# Revit family: Faucet-Single_Control-American_Standard-Colony_Pro-707500X_Series
name_source: partatom
category: Plumbing Fixtures
units: mm (PartAtom-declared; Revit-internal decimal feet)

## family parameters
Always vertical = No
Cut with Voids When Loaded = No
OmniClass Number = 23.45.55.14
OmniClass Title = Single Faucets
Part Type = Normal
Room Calculation Point = No
Round Connector Dimension = Use Diameter
Shared = Yes
Work Plane-Based = Yes

## types (12) — shared parameters
ADA Compliant = Yes
Assembly Code = D2020300
CEC Compliant = Yes
CW Connection = No
CWFU = 1.5
CalGreen Compliant = Yes
Compliance Certifications = These products meet or exceed the following codes and standards: ANSI A117.1, ASME A112.18.1,CSA B125.1,NSF 61/Section 9,NSF 372
Default Elevation = 0"
Drain Depth = 3"
Drain Width = 3"
Flow Rate = 1.2 gpm (4.5 L/min)
HW Connection = No
HWFU = 1.5
Height = 5 15/16"
Installation Type = Deck Mounted
Length = 6 3/8"
Manufacturer = American Standard
Product Documentation Link = https://americanstandard.box.com
Product Page URL = https://www.americanstandard-us.com
Revised Date = 09/23/2022
Tempered Water Connection = Yes
Tempered Water Connection Diameter = 3/8"
URL = http://www.americanstandard-us.com
Vent Connection = No
WFU = 2
Waste Connection = No
Width = 6"

## per-type parameters (varying)
| type | 50/50 Pop Up Drain | Description | Drain Visibility | Finish | Grid Drain | Material | Pop Up Drain | Pop-Up Hole & Rod |
| 7075000.002 | No | Colony® PRO 4-Inch Centerset Single-Handle Bathroom Faucet 1.2 gpm/4.5 L/min With Lever Handle | Yes | Metal-American Standard-002-Polished Chrome | No | Metal-American Standard-002-Polished Chrome | Yes | Yes |
| 7075000.295 | No | Colony® PRO 4-Inch Centerset Single-Handle Bathroom Faucet 1.2 gpm/4.5 L/min With Lever Handle | Yes | Metal-American Standard-295-Brushed Nickel | No | Metal-American Standard-295-Brushed Nickel | Yes | Yes |
| 7075000.278 | No | Colony® PRO 4-Inch Centerset Single-Handle Bathroom Faucet 1.2 gpm/4.5 L/min With Lever Handle | Yes | Metal-American Standard-278-Legacy Bronze | No | Metal-American Standard-278-Legacy Bronze | Yes | Yes |
| 7075002.002 | Yes | Colony® PRO 4-Inch Centerset Single-Handle Bathroom Faucet 1.2 gpm/4.5 Lpm With Lever Handle | Yes | Metal-American Standard-002-Polished Chrome | No | Metal-American Standard-002-Polished Chrome | No | Yes |
| 7075002.295 | Yes | Colony® PRO 4-Inch Centerset Single-Handle Bathroom Faucet 1.2 gpm/4.5 Lpm With Lever Handle | Yes | Metal-American Standard-295-Brushed Nickel | No | Metal-American Standard-295-Brushed Nickel | No | Yes |
| 7075002.278 | Yes | Colony® PRO 4-Inch Centerset Single-Handle Bathroom Faucet 1.2 gpm/4.5 Lpm With Lever Handle | Yes | Metal-American Standard-278-Legacy Bronze | No | Metal-American Standard-278-Legacy Bronze | No | Yes |
| 7075004.002 | No | Colony® PRO 4-Inch Centerset Single-Handle Bathroom Faucet 1.2 gpm/4.5 Lpm Less Drain With Lever Handle | No | Metal-American Standard-002-Polished Chrome | No | Metal-American Standard-002-Polished Chrome | No | No |
| 7075004.295 | No | Colony® PRO 4-Inch Centerset Single-Handle Bathroom Faucet 1.2 gpm/4.5 Lpm Less Drain With Lever Handle | No | Metal-American Standard-295-Brushed Nickel | No | Metal-American Standard-295-Brushed Nickel | No | No |
| 7075005.002 | No | Colony® PRO 4-Inch Centerset Single-Handle Bathroom Faucet 1.2 gpm/4.5 Lpm Less Drain With Lever Handle | No | Metal-American Standard-002-Polished Chrome | No | Metal-American Standard-002-Polished Chrome | No | Yes |
| 7075005.295 | No | Colony® PRO 4-Inch Centerset Single-Handle Bathroom Faucet 1.2 gpm/4.5 Lpm Less Drain With Lever Handle | No | Metal-American Standard-295-Brushed Nickel | No | Metal-American Standard-295-Brushed Nickel | No | Yes |
| 7075005.278 | No | Colony® PRO 4-Inch Centerset Single-Handle Bathroom Faucet 1.2 gpm/4.5 Lpm Less Drain With Lever Handle | No | Metal-American Standard-278-Legacy Bronze | No | Metal-American Standard-278-Legacy Bronze | No | Yes |
| 7075006.002 | No | Colony® PRO 4-Inch Centerset Single-Handle Bathroom Faucet 1.2 gpm/4.5 L/min With Grid Drain and Lever Handle | Yes | Metal-American Standard-002-Polished Chrome | Yes | Metal-American Standard-002-Polished Chrome | No | No |

note: column(s) folded — value = type name in every type: Model

## geometry (parser evidence)
native form markers: Sweep x5
no freeform markers — native parametric forms only
